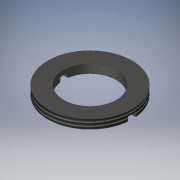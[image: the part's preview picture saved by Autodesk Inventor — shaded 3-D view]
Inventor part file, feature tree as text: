
AUTODESK INVENTOR PART (.ipt)
format: ipt  version: 2018.3 (Build 223285000, 285)  size: 124,928 bytes
history: native  units: mm
features: imported_body x1, thread x1
ambient origin geometry x8: Origin, YZ Plane, XZ Plane, XY Plane, X Axis, Y Axis, Z Axis, Center Point
bodies: Solid1 (feature_tree)
feature tree (2):
  imported_body  "Base1"
  thread  "Thread1"  [1 undecoded]
note: 1 required parameter value undecoded (feature->parameter linkage not recoverable at this tier; creation-order binding heuristic only, values carry confidence <= 0.55)
